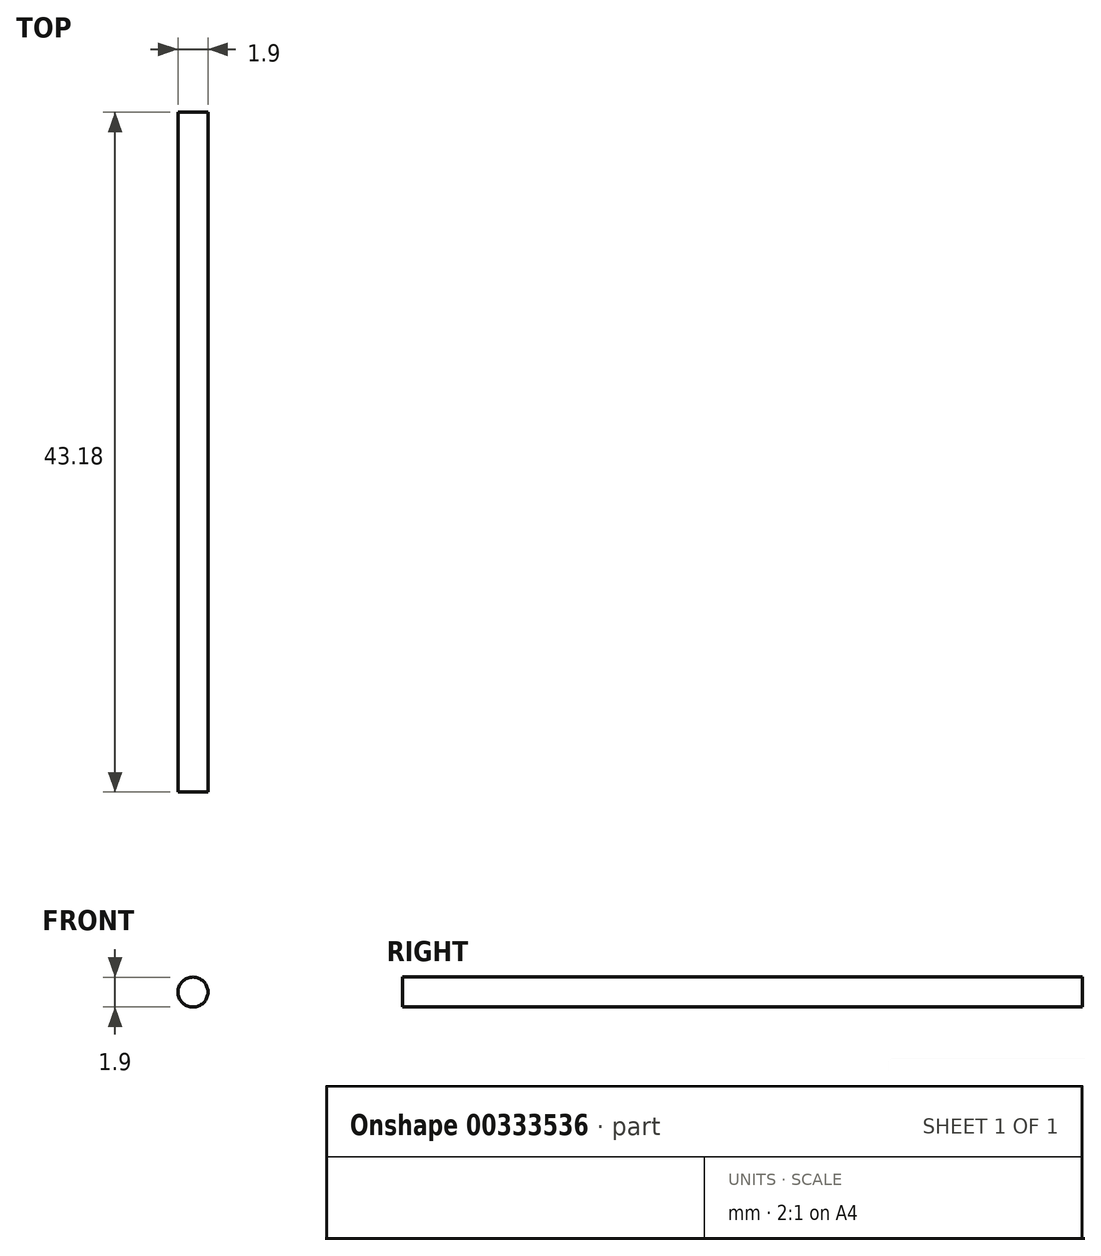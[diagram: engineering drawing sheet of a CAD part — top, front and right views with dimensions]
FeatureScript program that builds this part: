
annotation { "Feature Type Name" : "Feature", "Feature Type Description" : "" }
export const myFeature = defineFeature(function(context is Context, id is Id, definition is map)
    precondition{}
    {
        {
            var Q0;
            Q0=qCreatedBy(makeId("Front.planeOp"),FACE);
            var sketch = newSketch(context, id + "F0", { "sketchPlane" : qUnion([Q0])});
            skCircle(sketch, "E0", {"center": v(0, 0) * mm, "radius": 0.95 * mm});
            skSolve(sketch);
        }
        {
            var Q0;
            Q0 = qSketchRegion(id + "F0", true);
            extrude(context, id + "F1", {"entities" : qUnion([Q0]), "depth" : 43.18 * mm, "offsetDistance" : 25.4 * mm, "symmetric" : true});
        }
    });
